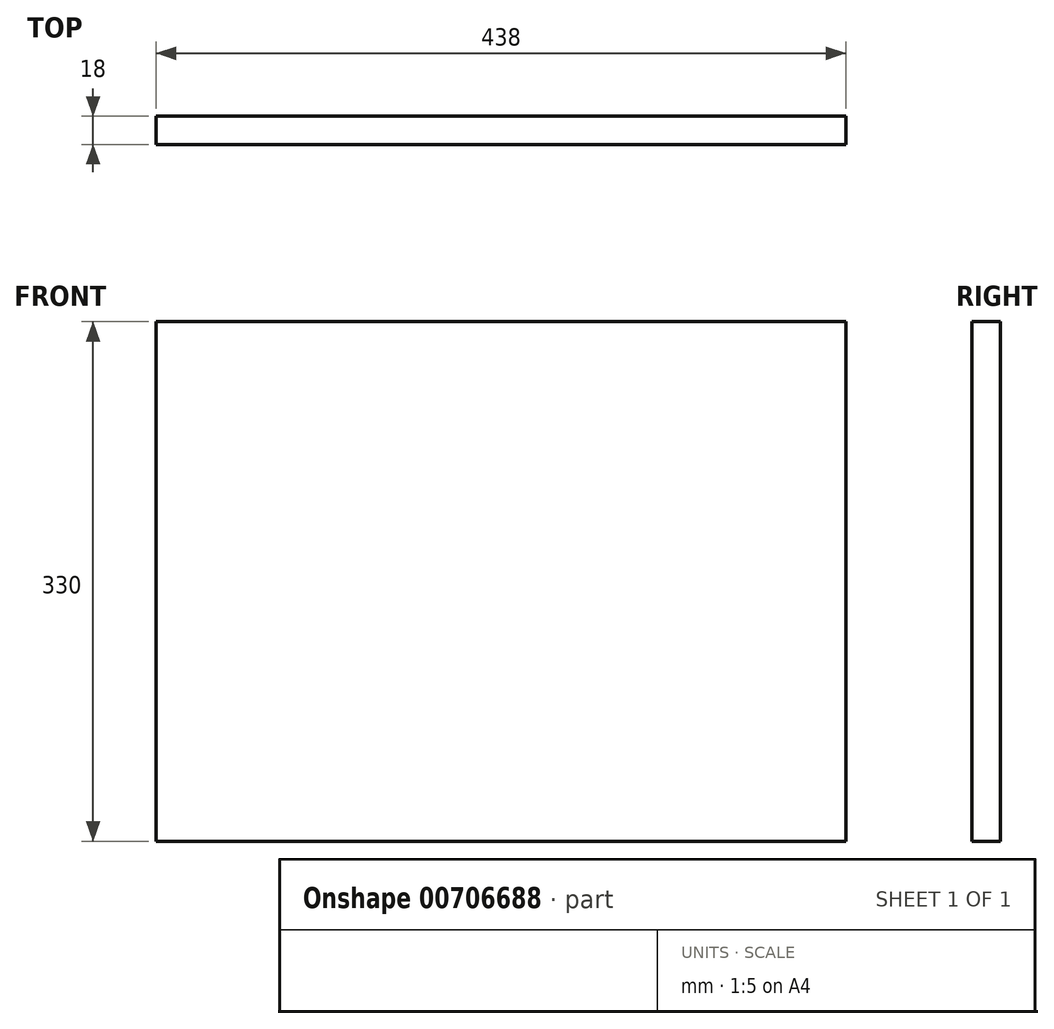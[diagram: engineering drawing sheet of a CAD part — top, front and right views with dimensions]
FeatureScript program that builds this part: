
annotation { "Feature Type Name" : "Feature", "Feature Type Description" : "" }
export const myFeature = defineFeature(function(context is Context, id is Id, definition is map)
    precondition{}
    {
        {
            var Q0;
            Q0=qCreatedBy(makeId("Front.planeOp"),FACE);
            var sketch = newSketch(context, id + "F0", { "sketchPlane" : qUnion([Q0])});
            skLineSegment(sketch, "E0.bottom", {"start": v(-219, -165) * mm, "end": v(219, -165) * mm});
            skLineSegment(sketch, "E0.top", {"start": v(-219, 165) * mm, "end": v(219, 165) * mm});
            skLineSegment(sketch, "E0.left", {"start": v(-219, -165) * mm, "end": v(-219, 165) * mm});
            skLineSegment(sketch, "E0.right", {"start": v(219, -165) * mm, "end": v(219, 165) * mm});
            skPoint(sketch, "E0.middle", {"position": v(0, 0) * mm});
            skSolve(sketch);
        }
        {
            var Q0;
            Q0=makeQuery(id+"F0.imprint","IMPRINT",FACE,{"disambiguationData":[TD([[makeQuery(id+"F0.imprint","IMPRINT",EDGE,{"derivedFrom":sQuery(id+"F0.wireOp",EDGE,"E0.bottom")}),1.0]])]});
            extrude(context, id + "F1", {"entities" : qUnion([Q0]), "depth" : 18 * mm, "offsetDistance" : 25 * mm, "symmetric" : true});
        }
    });
